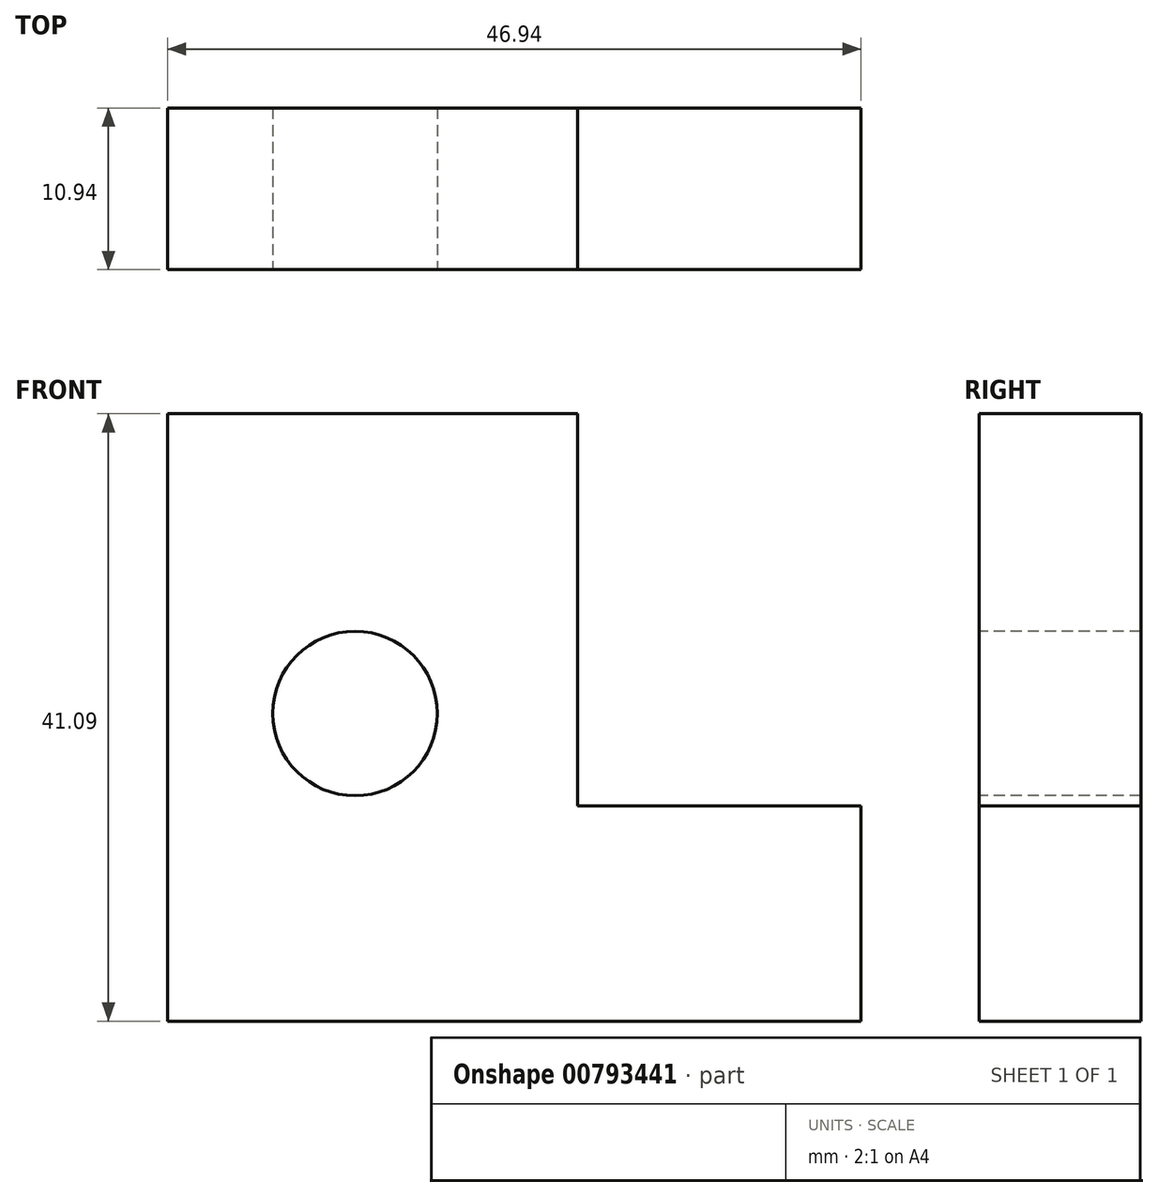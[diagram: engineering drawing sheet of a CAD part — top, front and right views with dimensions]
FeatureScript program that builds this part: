
annotation { "Feature Type Name" : "Feature", "Feature Type Description" : "" }
export const myFeature = defineFeature(function(context is Context, id is Id, definition is map)
    precondition{}
    {
        {
            var Q0;
            Q0=qCreatedBy(makeId("Front.planeOp"),FACE);
            var sketch = newSketch(context, id + "F0", { "sketchPlane" : qUnion([Q0])});
            skLineSegment(sketch, "E0", {"start": v(0, 0) * mm, "end": v(0, 41.1) * mm});
            skLineSegment(sketch, "E1", {"start": v(0, 41.1) * mm, "end": v(27.75, 41.1) * mm});
            skLineSegment(sketch, "E2", {"start": v(27.75, 41.1) * mm, "end": v(27.75, 14.56) * mm});
            skLineSegment(sketch, "E3", {"start": v(27.75, 14.56) * mm, "end": v(46.94, 14.56) * mm});
            skLineSegment(sketch, "E4", {"start": v(46.94, 14.56) * mm, "end": v(46.94, 0) * mm});
            skLineSegment(sketch, "E5", {"start": v(46.94, 0) * mm, "end": v(0, 0) * mm});
            skSolve(sketch);
        }
        {
            var Q0;
            Q0=qCreatedBy(makeId("Front.planeOp"),FACE);
            var sketch = newSketch(context, id + "F1", { "sketchPlane" : qUnion([Q0])});
            skCircle(sketch, "E6", {"center": v(12.7, 20.81) * mm, "radius": 5.56 * mm});
            skSolve(sketch);
        }
        {
            var Q0;
            Q0=makeQuery(id+"F0.imprint","IMPRINT",FACE,{"disambiguationData":[TD([[makeQuery(id+"F0.imprint","IMPRINT",EDGE,{"derivedFrom":sQuery(id+"F0.wireOp",EDGE,"E0")}),-1.0]])]});
            var Q1;
            Q1=makeQuery(id+"F1.imprint","IMPRINT",FACE,{"disambiguationData":[TD([[makeQuery(id+"F1.imprint","IMPRINT",EDGE,{"derivedFrom":sQuery(id+"F1.wireOp",EDGE,"E6")}),1.0]])]});
            extrude(context, id + "F2", {"entities" : qUnion([Q0, Q1]), "oppositeDirection" : true, "depth" : 10.94 * mm, "offsetDistance" : 25 * mm});
        }
    });
